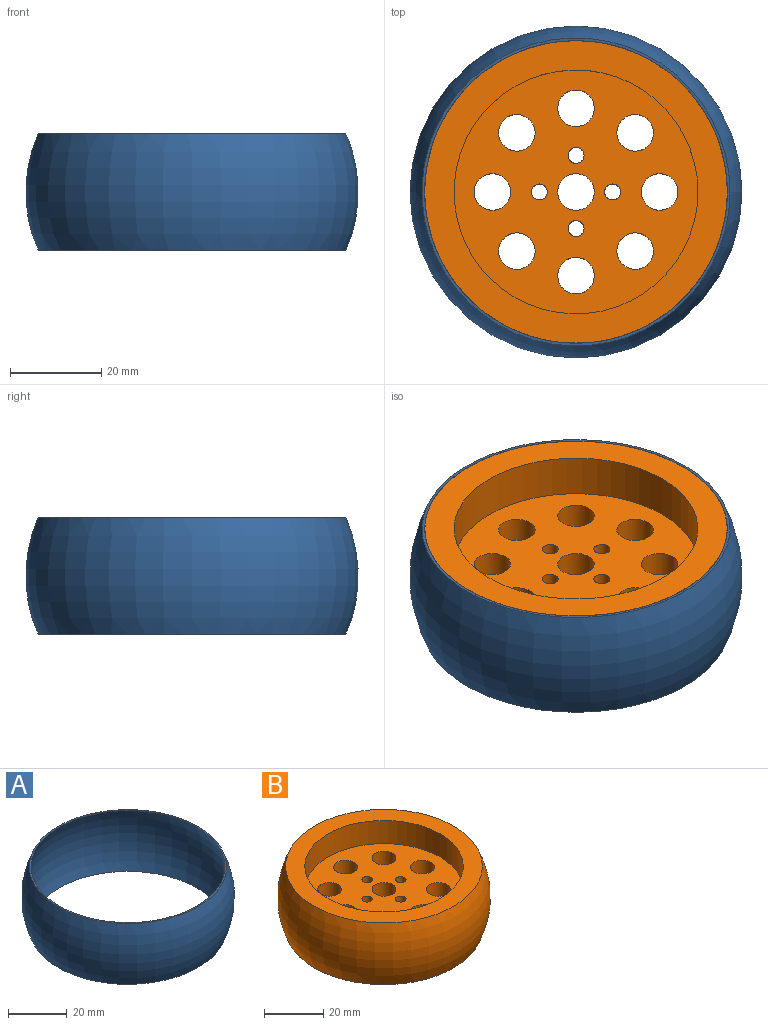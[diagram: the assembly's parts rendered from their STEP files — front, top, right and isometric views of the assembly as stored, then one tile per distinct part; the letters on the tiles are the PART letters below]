
ASSEMBLY  parts=2 mates=1
PART A: 4 faces, bbox 72.7x72.7x25.4 mm
  f0: plane 67.36x67.36mm, normal (0,0,1), area 121.9mm2, adj f1,f3
  f1: torus R=4.75mm, axis (0,0,1), area 5738.5mm2, adj f0,f2
  f2: plane 67.36x67.36mm, normal (0,0,-1), area 121.9mm2, adj f1,f3
  f3: torus R=4.78mm, axis (0,0,1), area 5823mm2, adj f0,f2
PART B: 20 faces, bbox 68.9x66.2x25.4 mm
  f0: plane 66.2x66.2mm, normal (0,0,1), area 1207.2mm2, adj f16,f19
  f1: plane 66.2x66.2mm, normal (0,0,-1), area 1207.2mm2, adj f15,f19
  f2: cylinder r=4mm len=8mm, axis (0,0,1), area 159.6mm2, adj f17,f18
  f3: cylinder r=4mm len=8mm, axis (0,0,1), area 159.6mm2, adj f17,f18
  f4: cylinder r=4mm len=8mm, axis (0,0,1), area 159.6mm2, adj f17,f18
  f5: cylinder r=4mm len=8mm, axis (0,0,1), area 159.6mm2, adj f17,f18
  f6: cylinder r=4mm len=8mm, axis (0,0,1), area 159.6mm2, adj f17,f18
  f7: cylinder r=4mm len=8mm, axis (0,0,1), area 159.6mm2, adj f17,f18
  f8: cylinder r=4mm len=8mm, axis (0,0,1), area 159.6mm2, adj f17,f18
  f9: cylinder r=4mm len=8mm, axis (0,0,1), area 159.6mm2, adj f17,f18
  f10: cylinder r=1.75mm len=6.35mm, axis (0,0,1), area 69.8mm2, adj f17,f18
  f11: cylinder r=1.75mm len=6.35mm, axis (0,0,1), area 69.8mm2, adj f17,f18
  f12: cylinder r=1.75mm len=6.35mm, axis (0,0,1), area 69.8mm2, adj f17,f18
  f13: cylinder r=1.75mm len=6.35mm, axis (0,0,1), area 69.8mm2, adj f17,f18
  f14: cylinder r=4mm len=8mm, axis (0,0,1), area 159.6mm2, adj f17,f18
  f15: cylinder r=26.67mm len=53.34mm, axis (0,0,-1), area 1596.1mm2, adj f1,f18
  f16: cylinder r=26.67mm len=53.34mm, axis (0,0,1), area 1596.1mm2, adj f0,f17
  f17: plane 53.34x53.34mm, normal (0,0,1), area 1743.7mm2, adj f2,f3,f4,f5,f6,f7,f8,f9
  f18: plane 53.34x53.34mm, normal (0,0,-1), area 1743.7mm2, adj f2,f3,f4,f5,f6,f7,f8,f9
  f19: torus R=4.75mm, axis (0,0,-1), area 5738.5mm2, adj f0,f1
PLACE A t=(40.52,0.93,-22.54)mm
PLACE B t=(40.52,0.93,-22.54)mm fixed
MATE fastened A.f1 <-> B.f14  axis (0,0,1) through (0.64,-0.84,12.41)mm
